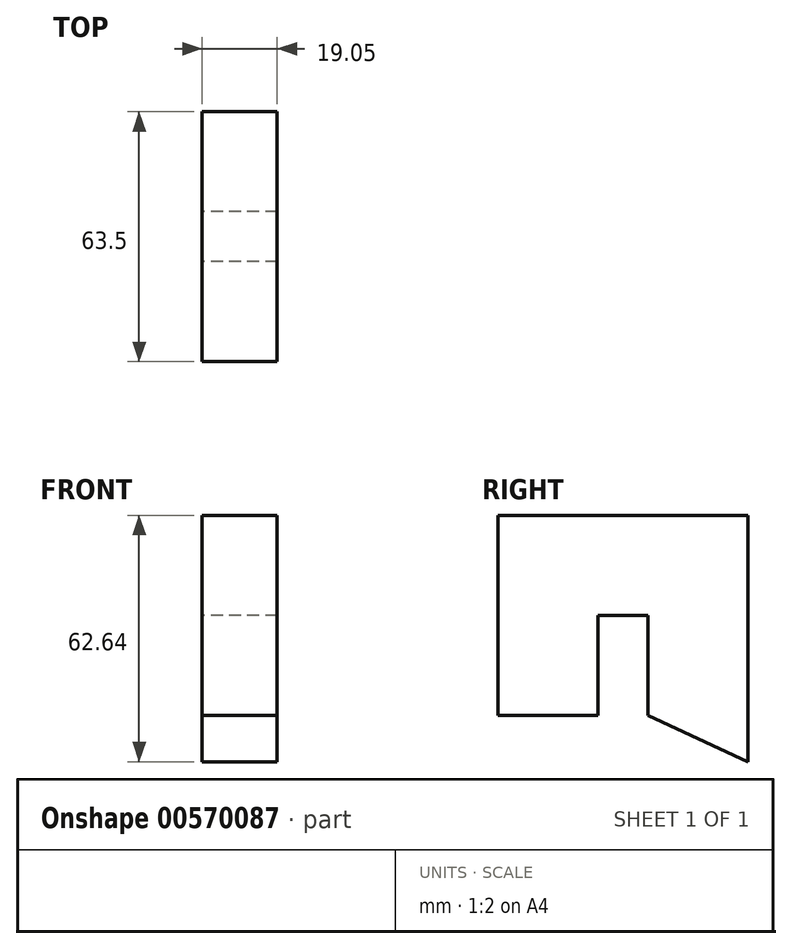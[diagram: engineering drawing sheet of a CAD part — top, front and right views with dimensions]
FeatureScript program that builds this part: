
annotation { "Feature Type Name" : "Feature", "Feature Type Description" : "" }
export const myFeature = defineFeature(function(context is Context, id is Id, definition is map)
    precondition{}
    {
        {
            var Q0;
            Q0=qCreatedBy(makeId("Right.planeOp"),FACE);
            var sketch = newSketch(context, id + "F0", { "sketchPlane" : qUnion([Q0])});
            skLineSegment(sketch, "E0", {"start": v(0, 0) * mm, "end": v(25.4, 0) * mm});
            skLineSegment(sketch, "E1", {"start": v(25.4, 0) * mm, "end": v(25.4, 50.8) * mm});
            skLineSegment(sketch, "E2", {"start": v(25.4, 50.8) * mm, "end": v(0, 50.8) * mm});
            skLineSegment(sketch, "E3", {"start": v(0, 0) * mm, "end": v(0, 25.4) * mm});
            skLineSegment(sketch, "E4", {"start": v(0, 25.4) * mm, "end": v(-12.7, 25.4) * mm});
            skLineSegment(sketch, "E5", {"start": v(-12.7, 25.4) * mm, "end": v(-12.7, 0) * mm});
            skLineSegment(sketch, "E6", {"start": v(-12.7, 0) * mm, "end": v(-38.1, -11.84) * mm});
            skLineSegment(sketch, "E7", {"start": v(0, 50.8) * mm, "end": v(-38.1, 50.8) * mm});
            skLineSegment(sketch, "E8", {"start": v(-38.1, 50.8) * mm, "end": v(-38.1, -11.84) * mm});
            skSolve(sketch);
        }
        {
            var Q0;
            Q0 = qSketchRegion(id + "F0", true);
            extrude(context, id + "F1", {"entities" : qUnion([Q0]), "oppositeDirection" : true, "depth" : 19.05 * mm, "offsetDistance" : 25.4 * mm});
        }
        {
            var Q0;
            Q0=makeQuery(id+"F1.opExtrude","SWEPT_BODY",BODY,{"disambiguationData":[OSD([sQuery(id+"F0.wireOp",EDGE,"E0"),sQuery(id+"F0.wireOp",EDGE,"E1"),sQuery(id+"F0.wireOp",EDGE,"E2"),sQuery(id+"F0.wireOp",EDGE,"E3"),sQuery(id+"F0.wireOp",EDGE,"E4"),sQuery(id+"F0.wireOp",EDGE,"E5"),sQuery(id+"F0.wireOp",EDGE,"E6"),sQuery(id+"F0.wireOp",EDGE,"E7"),sQuery(id+"F0.wireOp",EDGE,"E8")])]});
            var Q1;
            Q1=makeQuery(id+"F1.opExtrude","CAP_EDGE",EDGE,{"disambiguationData":[OSD([sQuery(id+"F0.wireOp",EDGE,"E1")])],"isStart":true});
            transform(context, id + "F2", {"entities" : qUnion([Q0]), "transformType" : TransformType.ROTATION, "transformAxis" : qUnion([Q1]), "angle" : 180 * degree, "makeCopy" : false});
        }
    });
